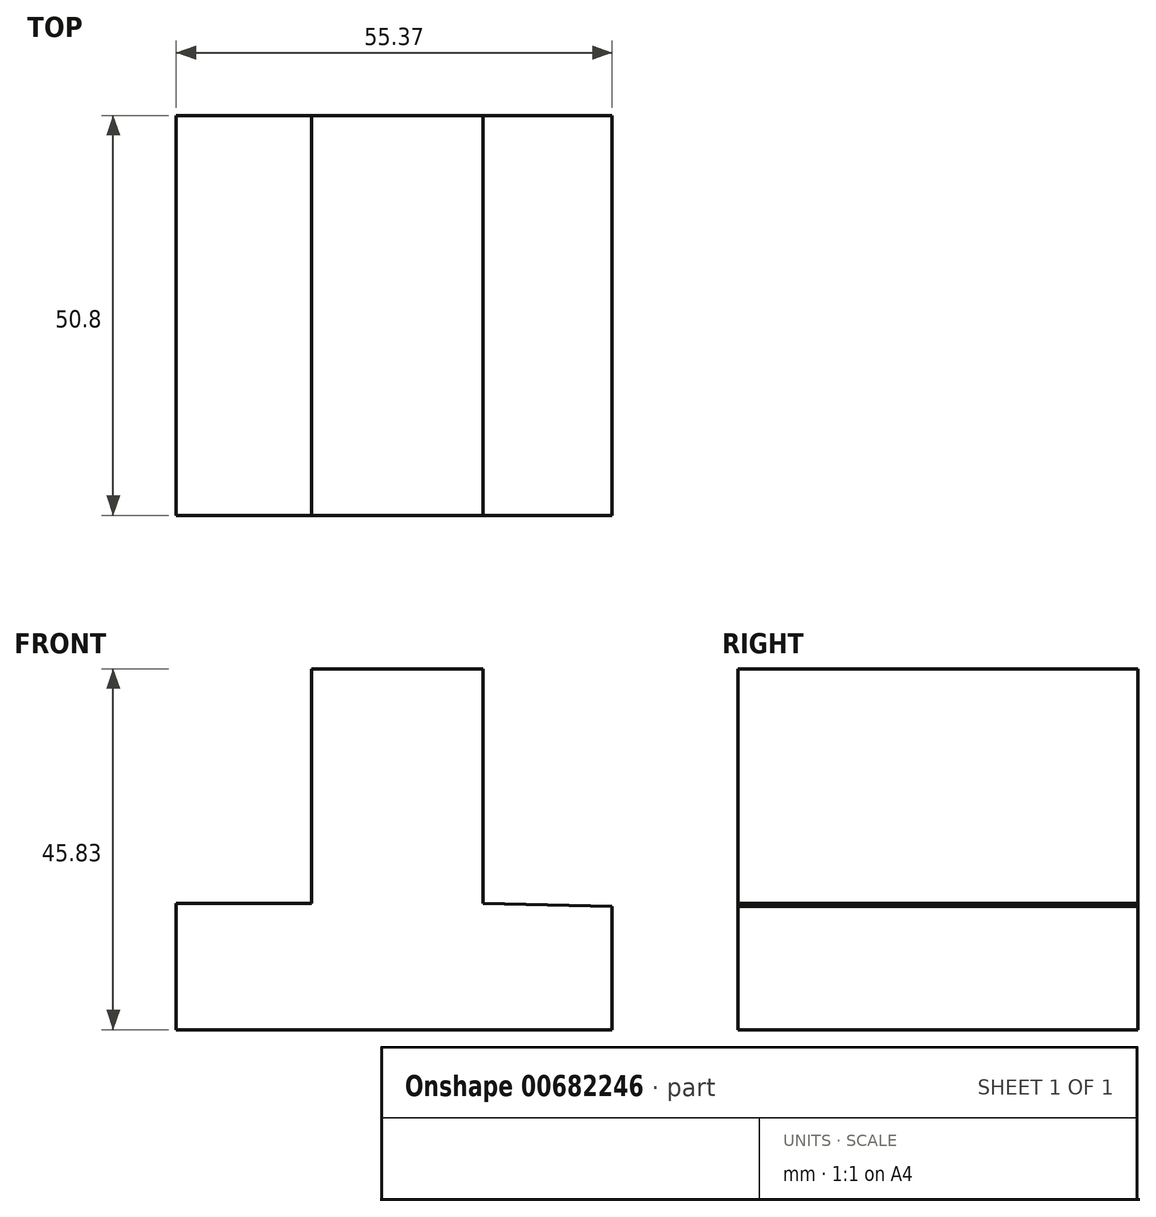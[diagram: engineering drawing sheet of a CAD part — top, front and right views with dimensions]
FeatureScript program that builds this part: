
annotation { "Feature Type Name" : "Feature", "Feature Type Description" : "" }
export const myFeature = defineFeature(function(context is Context, id is Id, definition is map)
    precondition{}
    {
        {
            var Q0;
            Q0=qCreatedBy(makeId("Front.planeOp"),FACE);
            var sketch = newSketch(context, id + "F0", { "sketchPlane" : qUnion([Q0])});
            skLineSegment(sketch, "E0", {"start": v(-71.9, 19.57) * mm, "end": v(-71.9, 3.53) * mm});
            skLineSegment(sketch, "E1", {"start": v(-71.9, 3.53) * mm, "end": v(-16.52, 3.53) * mm});
            skLineSegment(sketch, "E2", {"start": v(-16.52, 3.53) * mm, "end": v(-16.52, 19.2) * mm});
            skLineSegment(sketch, "E3", {"start": v(-71.9, 19.57) * mm, "end": v(-54.7, 19.57) * mm});
            skLineSegment(sketch, "E4", {"start": v(-54.7, 19.57) * mm, "end": v(-54.7, 49.36) * mm});
            skLineSegment(sketch, "E5", {"start": v(-54.7, 49.36) * mm, "end": v(-32.94, 49.36) * mm});
            skLineSegment(sketch, "E6", {"start": v(-32.94, 49.36) * mm, "end": v(-32.94, 19.57) * mm});
            skLineSegment(sketch, "E7", {"start": v(-32.94, 19.57) * mm, "end": v(-16.52, 19.2) * mm});
            skSolve(sketch);
        }
        {
            var Q0;
            Q0 = qSketchRegion(id + "F0", true);
            extrude(context, id + "F1", {"entities" : qUnion([Q0]), "depth" : 50.8 * mm, "offsetDistance" : 25.4 * mm});
        }
    });
